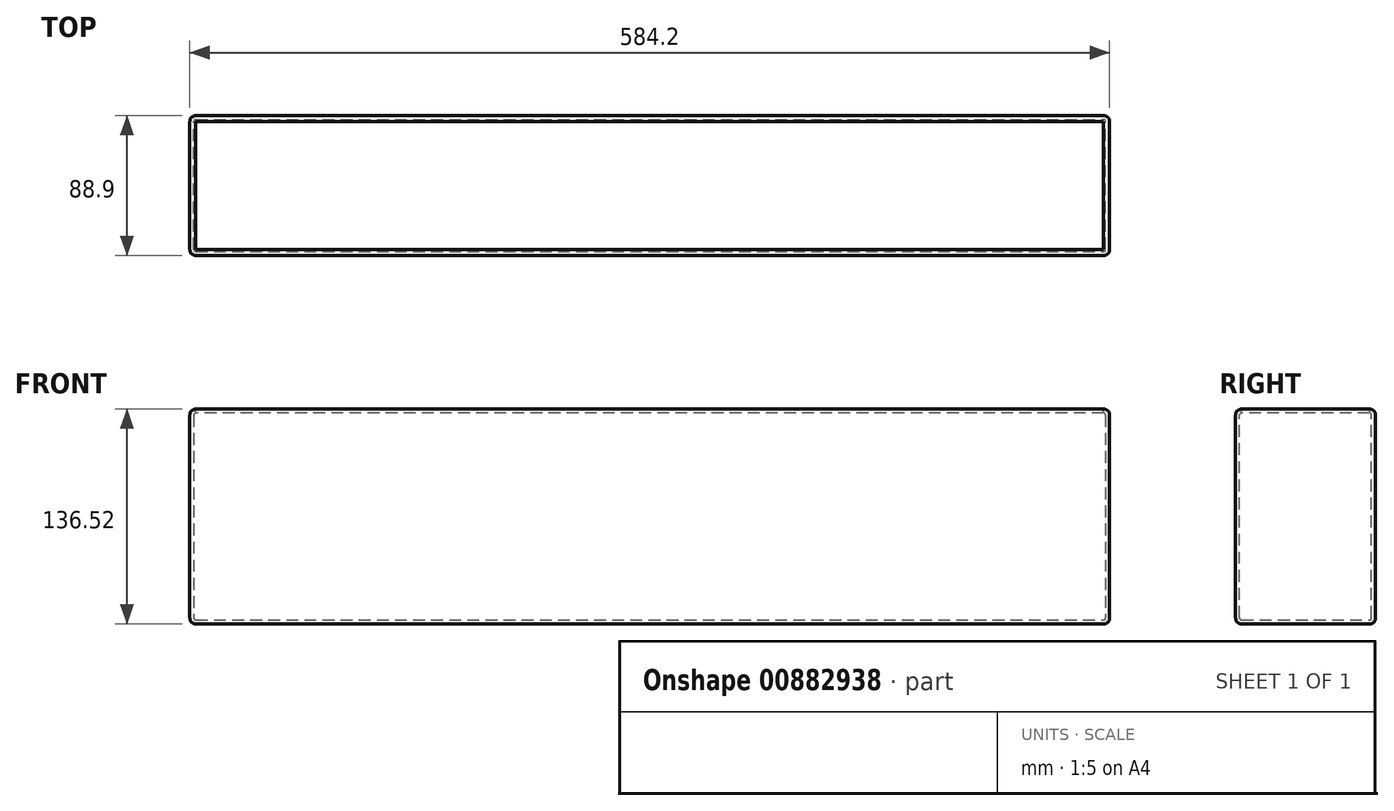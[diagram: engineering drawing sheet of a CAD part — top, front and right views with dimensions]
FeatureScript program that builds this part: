
annotation { "Feature Type Name" : "Feature", "Feature Type Description" : "" }
export const myFeature = defineFeature(function(context is Context, id is Id, definition is map)
    precondition{}
    {
        {
            var Q0;
            Q0=qCreatedBy(makeId("Front.planeOp"),FACE);
            var sketch = newSketch(context, id + "F0", { "sketchPlane" : qUnion([Q0])});
            skLineSegment(sketch, "E0.bottom", {"start": v(-292.1, 68.26) * mm, "end": v(292.1, 68.26) * mm});
            skLineSegment(sketch, "E0.top", {"start": v(-292.1, -68.26) * mm, "end": v(292.1, -68.26) * mm});
            skLineSegment(sketch, "E0.left", {"start": v(-292.1, 68.26) * mm, "end": v(-292.1, -68.26) * mm});
            skLineSegment(sketch, "E0.right", {"start": v(292.1, 68.26) * mm, "end": v(292.1, -68.26) * mm});
            skPoint(sketch, "E0.middle", {"position": v(0, 0) * mm});
            skSolve(sketch);
        }
        {
            var Q0;
            Q0=makeQuery(id+"F0.imprint","IMPRINT",FACE,{"disambiguationData":[TD([[makeQuery(id+"F0.imprint","IMPRINT",EDGE,{"derivedFrom":sQuery(id+"F0.wireOp",EDGE,"E0.bottom")}),-1.0]])]});
            extrude(context, id + "F1", {"entities" : qUnion([Q0]), "depth" : 88.9 * mm, "offsetDistance" : 25.4 * mm});
        }
        {
            var Q0;
            Q0=makeQuery(id+"F1.opExtrude","SWEPT_EDGE",EDGE,{"disambiguationData":[OSD([sQuery(id+"F0.wireOp",EDGE,"E0.bottom"),sQuery(id+"F0.wireOp",EDGE,"E0.left")])]});
            var Q1;
            Q1=makeQuery(id+"F1.opExtrude","CAP_EDGE",EDGE,{"disambiguationData":[OSD([sQuery(id+"F0.wireOp",EDGE,"E0.bottom")])],"isStart":true});
            var Q2;
            Q2=makeQuery(id+"F1.opExtrude","CAP_EDGE",EDGE,{"disambiguationData":[OSD([sQuery(id+"F0.wireOp",EDGE,"E0.bottom")])],"isStart":false});
            var Q3;
            Q3=makeQuery(id+"F1.opExtrude","CAP_EDGE",EDGE,{"disambiguationData":[OSD([sQuery(id+"F0.wireOp",EDGE,"E0.left")])],"isStart":false});
            var Q4;
            Q4=makeQuery(id+"F1.opExtrude","CAP_EDGE",EDGE,{"disambiguationData":[OSD([sQuery(id+"F0.wireOp",EDGE,"E0.top")])],"isStart":false});
            var Q5;
            Q5=makeQuery(id+"F1.opExtrude","CAP_EDGE",EDGE,{"disambiguationData":[OSD([sQuery(id+"F0.wireOp",EDGE,"E0.right")])],"isStart":false});
            var Q6;
            Q6=makeQuery(id+"F1.opExtrude","SWEPT_EDGE",EDGE,{"disambiguationData":[OSD([sQuery(id+"F0.wireOp",EDGE,"E0.bottom"),sQuery(id+"F0.wireOp",EDGE,"E0.right")])]});
            var Q7;
            Q7=makeQuery(id+"F1.opExtrude","CAP_EDGE",EDGE,{"disambiguationData":[OSD([sQuery(id+"F0.wireOp",EDGE,"E0.left")])],"isStart":true});
            var Q8;
            Q8=makeQuery(id+"F1.opExtrude","SWEPT_EDGE",EDGE,{"disambiguationData":[OSD([sQuery(id+"F0.wireOp",EDGE,"E0.top"),sQuery(id+"F0.wireOp",EDGE,"E0.left")])]});
            var Q9;
            Q9=makeQuery(id+"F1.opExtrude","CAP_EDGE",EDGE,{"disambiguationData":[OSD([sQuery(id+"F0.wireOp",EDGE,"E0.top")])],"isStart":true});
            var Q10;
            Q10=makeQuery(id+"F1.opExtrude","CAP_EDGE",EDGE,{"disambiguationData":[OSD([sQuery(id+"F0.wireOp",EDGE,"E0.right")])],"isStart":true});
            var Q11;
            Q11=makeQuery(id+"F1.opExtrude","SWEPT_EDGE",EDGE,{"disambiguationData":[OSD([sQuery(id+"F0.wireOp",EDGE,"E0.top"),sQuery(id+"F0.wireOp",EDGE,"E0.right")])]});
            fillet(context, id + "F2", {"entities" : qUnion([Q0, Q1, Q2, Q3, Q4, Q5, Q6, Q7, Q8, Q9, Q10, Q11]), "radius" : 3.8 * mm, "tangentPropagation" : true, "allowEdgeOverflow" : false});
        }
        {
            var Q0;
            Q0=makeQuery(id+"F1.opExtrude","SWEPT_FACE",FACE,{"disambiguationData":[OSD([sQuery(id+"F0.wireOp",EDGE,"E0.bottom")])]});
            shell(context, id + "F3", {"entities" : qUnion([Q0]), "thickness" : 2.54 * mm});
        }
    });
